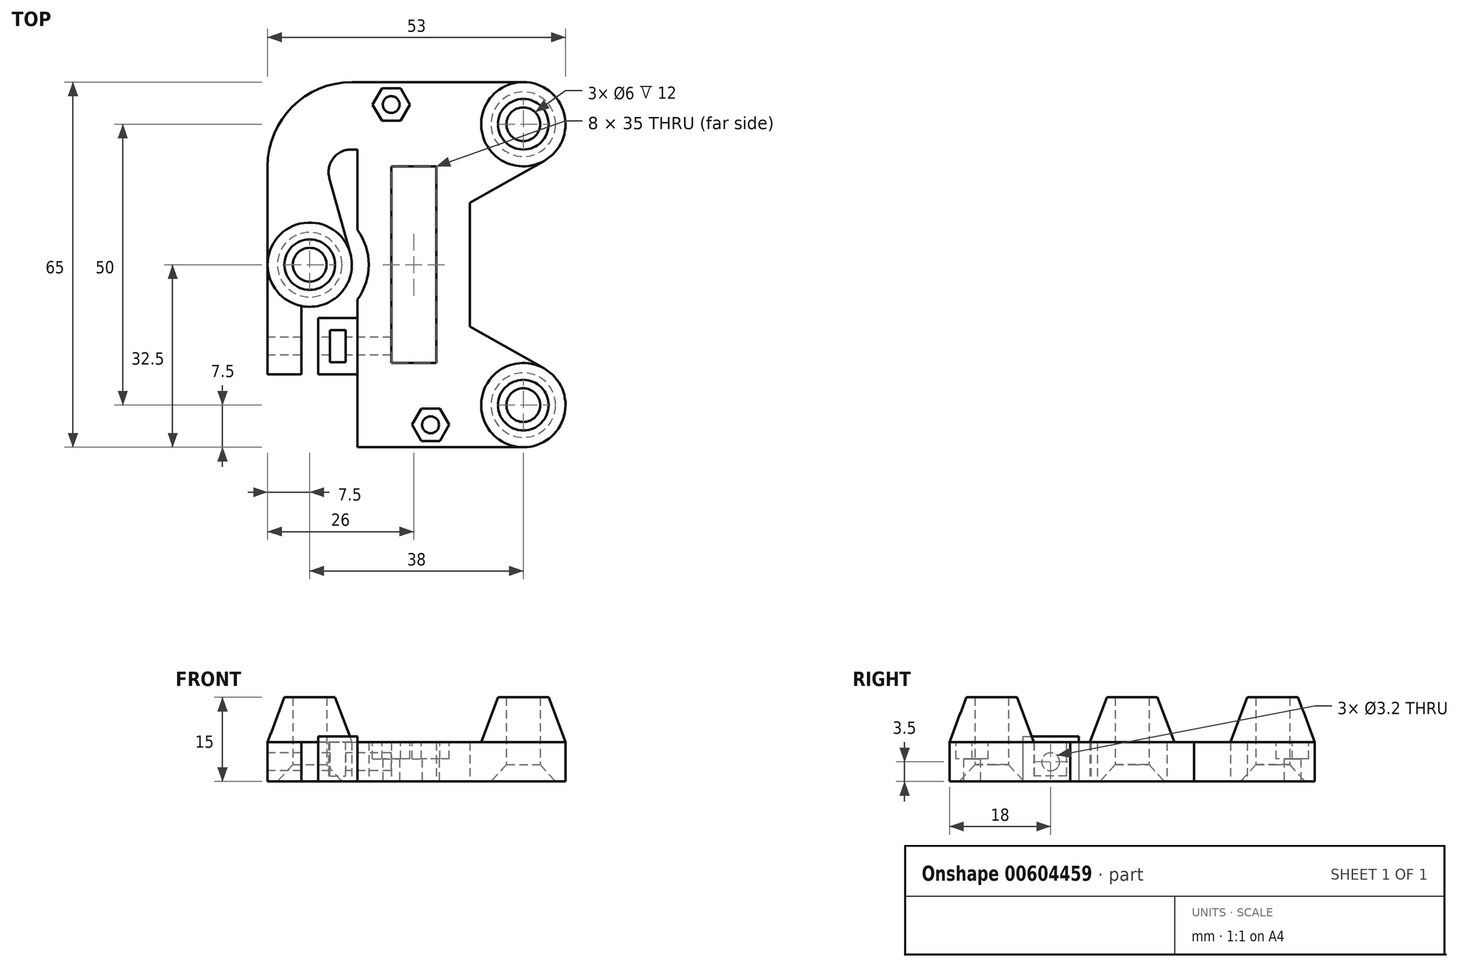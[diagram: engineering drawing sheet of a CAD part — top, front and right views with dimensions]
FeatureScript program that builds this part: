
annotation { "Feature Type Name" : "Feature", "Feature Type Description" : "" }
export const myFeature = defineFeature(function(context is Context, id is Id, definition is map)
    precondition{}
    {
        {
            var Q0;
            Q0=qCreatedBy(makeId("Top.planeOp"),FACE);
            var sketch = newSketch(context, id + "F0", { "sketchPlane" : qUnion([Q0])});
            skLineSegment(sketch, "E0.bottom", {"start": v(0, 0) * mm, "end": v(20, 0) * mm});
            skLineSegment(sketch, "E0.top", {"start": v(0, 65) * mm, "end": v(20, 65) * mm});
            skLineSegment(sketch, "E0.left", {"start": v(0, 0) * mm, "end": v(0, 26.34) * mm});
            skLineSegment(sketch, "E0.right", {"start": v(20, 0) * mm, "end": v(20, 65) * mm});
            skLineSegment(sketch, "E1.bottom", {"start": v(6, 50) * mm, "end": v(14, 50) * mm});
            skLineSegment(sketch, "E1.top", {"start": v(6, 15) * mm, "end": v(14, 15) * mm});
            skLineSegment(sketch, "E1.left", {"start": v(6, 50) * mm, "end": v(6, 15) * mm});
            skLineSegment(sketch, "E1.right", {"start": v(14, 50) * mm, "end": v(14, 15) * mm});
            skLineSegment(sketch, "E2.bottom", {"start": v(-7, 23) * mm, "end": v(0, 23) * mm});
            skLineSegment(sketch, "E2.top", {"start": v(-7, 13) * mm, "end": v(0, 13) * mm});
            skLineSegment(sketch, "E2.left", {"start": v(-7, 23) * mm, "end": v(-7, 13) * mm});
            skLineSegment(sketch, "E2.right", {"start": v(0, 23) * mm, "end": v(0, 13) * mm});
            skCircle(sketch, "E3", {"center": v(29.5, 7.5) * mm, "radius": 3 * mm});
            skCircle(sketch, "E4", {"center": v(29.5, 57.5) * mm, "radius": 3 * mm});
            skCircle(sketch, "E5", {"center": v(-8.5, 32.5) * mm, "radius": 7.5 * mm});
            skCircle(sketch, "E6", {"center": v(29.5, 57.5) * mm, "radius": 7.5 * mm});
            skCircle(sketch, "E7", {"center": v(29.5, 7.5) * mm, "radius": 7.5 * mm});
            skLineSegment(sketch, "E8", {"start": v(20, 0) * mm, "end": v(29.5, 0) * mm});
            skLineSegment(sketch, "E9", {"start": v(20, 65) * mm, "end": v(29.5, 65) * mm});
            skLineSegment(sketch, "E10", {"start": v(-1.27, 34.5) * mm, "end": v(-5, 47.93) * mm});
            skLineSegment(sketch, "E11", {"start": v(-16, 13) * mm, "end": v(-16, 50) * mm});
            skCircle(sketch, "E12", {"center": v(-8.5, 32.5) * mm, "radius": 3 * mm});
            skLineSegment(sketch, "E13", {"start": v(-16, 13) * mm, "end": v(-10, 13) * mm});
            skLineSegment(sketch, "E14", {"start": v(-10, 13) * mm, "end": v(-10, 25.15) * mm});
            skLineSegment(sketch, "E15", {"start": v(-1, 65) * mm, "end": v(0, 65) * mm});
            skCircle(sketch, "E16", {"center": v(6, 61) * mm, "radius": 1.5 * mm});
            skCircle(sketch, "E17", {"center": v(13, 4) * mm, "radius": 1.5 * mm});
            skLineSegment(sketch, "E18", {"start": v(33.2, 50.97) * mm, "end": v(20, 43.5) * mm});
            skLineSegment(sketch, "E19", {"start": v(33.2, 14.03) * mm, "end": v(20, 21.5) * mm});
            skPoint(sketch, "E20.visualSharp", {"position": v(-16, 65) * mm});
            skArc(sketch, "E20.filletArc", {"start": v(-1, 65) * mm, "mid": v(-11.6, 60.6) * mm, "end": v(-16, 50) * mm});
            skLineSegment(sketch, "E21", {"start": v(-1.15, 53) * mm, "end": v(0, 53) * mm});
            skPoint(sketch, "E22", {"position": v(20, 32.5) * mm});
            skArc(sketch, "E23", {"start": v(0, 26.34) * mm, "mid": v(2, 32.5) * mm, "end": v(0, 38.66) * mm});
            skLineSegment(sketch, "E24", {"start": v(6, 32.5) * mm, "end": v(2, 32.5) * mm});
            skLineSegment(sketch, "E25.trimOffspring", {"start": v(0, 38.66) * mm, "end": v(0, 65) * mm});
            skPoint(sketch, "E26.visualSharp", {"position": v(-6.4, 53) * mm});
            skArc(sketch, "E26.filletArc", {"start": v(-1.15, 53) * mm, "mid": v(-4.33, 51.42) * mm, "end": v(-5, 47.93) * mm});
            skPoint(sketch, "E27", {"position": v(37, 57.5) * mm});
            skSolve(sketch);
        }
        {
            var Q0;
            Q0=qSketchRegion(id+"F0",true);
            extrude(context, id + "F1", {"entities" : qUnion([Q0]), "depth" : 7 * mm});
        }
        {
            var Q0;
            Q0=makeQuery(id+"F1.opExtrude","CAP_FACE",FACE,{"disambiguationData":[OSD([sQuery(id+"F0.wireOp",EDGE,"E0.bottom"),sQuery(id+"F0.wireOp",EDGE,"E0.top"),sQuery(id+"F0.wireOp",EDGE,"E0.left"),sQuery(id+"F0.wireOp",EDGE,"E0.right"),sQuery(id+"F0.wireOp",EDGE,"E1.bottom"),sQuery(id+"F0.wireOp",EDGE,"E1.top"),sQuery(id+"F0.wireOp",EDGE,"E1.left"),sQuery(id+"F0.wireOp",EDGE,"E1.right"),sQuery(id+"F0.wireOp",EDGE,"E2.bottom"),sQuery(id+"F0.wireOp",EDGE,"E2.top"),sQuery(id+"F0.wireOp",EDGE,"E2.left"),sQuery(id+"F0.wireOp",EDGE,"E3"),sQuery(id+"F0.wireOp",EDGE,"E4"),sQuery(id+"F0.wireOp",EDGE,"E5"),sQuery(id+"F0.wireOp",EDGE,"E6"),sQuery(id+"F0.wireOp",EDGE,"E7"),sQuery(id+"F0.wireOp",EDGE,"E8"),sQuery(id+"F0.wireOp",EDGE,"E9"),sQuery(id+"F0.wireOp",EDGE,"E10"),sQuery(id+"F0.wireOp",EDGE,"E11"),sQuery(id+"F0.wireOp",EDGE,"E12"),sQuery(id+"F0.wireOp",EDGE,"E13"),sQuery(id+"F0.wireOp",EDGE,"E14"),sQuery(id+"F0.wireOp",EDGE,"E16"),sQuery(id+"F0.wireOp",EDGE,"E17"),sQuery(id+"F0.wireOp",EDGE,"E18"),sQuery(id+"F0.wireOp",EDGE,"E19"),sQuery(id+"F0.wireOp",EDGE,"E20.filletArc"),sQuery(id+"F0.wireOp",EDGE,"E23"),sQuery(id+"F0.wireOp",EDGE,"E25.trimOffspring"),sQuery(id+"F0.wireOp",EDGE,"E26.filletArc")])],"isStart":false});
            cPlane(context, id + "F2", {"entities" : qUnion([Q0]), "cplaneType" : CPlaneType.OFFSET, "offset" : 0 * mm, "width" : 150 * mm, "height" : 150 * mm});
        }
        {
            var Q0;
            Q0=qCreatedBy(id+"F2.planeOp",FACE);
            var sketch = newSketch(context, id + "F3", { "sketchPlane" : qUnion([Q0])});
            skCircle(sketch, "E28.cCircle", {"center": v(13, 4) * mm, "radius": 2.88 * mm, "construction": true});
            skLineSegment(sketch, "E28.0", {"start": v(14.66, 1.13) * mm, "end": v(11.34, 1.12) * mm});
            skLineSegment(sketch, "E28.1", {"start": v(11.34, 1.12) * mm, "end": v(9.68, 4) * mm});
            skLineSegment(sketch, "E28.2", {"start": v(9.68, 4) * mm, "end": v(11.34, 6.88) * mm});
            skLineSegment(sketch, "E28.3", {"start": v(11.34, 6.88) * mm, "end": v(14.66, 6.88) * mm});
            skLineSegment(sketch, "E28.4", {"start": v(14.66, 6.87) * mm, "end": v(16.32, 4) * mm});
            skLineSegment(sketch, "E28.5", {"start": v(16.32, 4) * mm, "end": v(14.66, 1.12) * mm});
            skPoint(sketch, "E28.0.midPoint", {"position": v(13, 1.13) * mm});
            skCircle(sketch, "E29.cCircle", {"center": v(6, 61) * mm, "radius": 2.88 * mm, "construction": true});
            skLineSegment(sketch, "E29.0", {"start": v(9.32, 61) * mm, "end": v(7.66, 58.13) * mm});
            skLineSegment(sketch, "E29.1", {"start": v(7.66, 58.12) * mm, "end": v(4.34, 58.12) * mm});
            skLineSegment(sketch, "E29.2", {"start": v(4.34, 58.12) * mm, "end": v(2.68, 61) * mm});
            skLineSegment(sketch, "E29.3", {"start": v(2.68, 61) * mm, "end": v(4.34, 63.87) * mm});
            skLineSegment(sketch, "E29.4", {"start": v(4.34, 63.88) * mm, "end": v(7.66, 63.88) * mm});
            skLineSegment(sketch, "E29.5", {"start": v(7.66, 63.88) * mm, "end": v(9.32, 61) * mm});
            skPoint(sketch, "E29.0.midPoint", {"position": v(8.49, 59.56) * mm});
            skSolve(sketch);
        }
        {
            var Q0;
            Q0=qSketchRegion(id+"F3",true);
            extrude(context, id + "F4", {"entities" : qUnion([Q0]), "operationType" : NewBodyOperationType.REMOVE, "oppositeDirection" : true, "depth" : 3 * mm});
        }
        {
            var Q0;
            Q0=qCreatedBy(id+"F2.planeOp",FACE);
            var sketch = newSketch(context, id + "F5", { "sketchPlane" : qUnion([Q0])});
            skLineSegment(sketch, "E30.bottom", {"start": v(-7, 13) * mm, "end": v(0, 13) * mm});
            skLineSegment(sketch, "E30.top", {"start": v(-7, 23) * mm, "end": v(0, 23) * mm});
            skLineSegment(sketch, "E30.left", {"start": v(-7, 13) * mm, "end": v(-7, 23) * mm});
            skLineSegment(sketch, "E30.right", {"start": v(0, 13) * mm, "end": v(0, 23) * mm});
            skSolve(sketch);
        }
        {
            var Q0;
            Q0=qSketchRegion(id+"F5",true);
            extrude(context, id + "F6", {"entities" : qUnion([Q0]), "operationType" : NewBodyOperationType.ADD, "depth" : 1 * mm});
        }
        {
            var Q0;
            Q0=makeQuery(id+"F6.opExtrude","CAP_FACE",FACE,{"disambiguationData":[OSD([sQuery(id+"F5.wireOp",EDGE,"E30.bottom"),sQuery(id+"F5.wireOp",EDGE,"E30.top"),sQuery(id+"F5.wireOp",EDGE,"E30.left"),sQuery(id+"F5.wireOp",EDGE,"E30.right")])],"isStart":false});
            cPlane(context, id + "F7", {"entities" : qUnion([Q0]), "cplaneType" : CPlaneType.OFFSET, "offset" : 0 * mm, "width" : 150 * mm, "height" : 150 * mm});
        }
        {
            var Q0;
            Q0=qCreatedBy(id+"F7.planeOp",FACE);
            var sketch = newSketch(context, id + "F8", { "sketchPlane" : qUnion([Q0])});
            skLineSegment(sketch, "E31.bottom", {"start": v(-4.87, 20.88) * mm, "end": v(-2.12, 20.88) * mm});
            skLineSegment(sketch, "E31.top", {"start": v(-4.87, 15.13) * mm, "end": v(-2.12, 15.13) * mm});
            skLineSegment(sketch, "E31.left", {"start": v(-4.87, 20.88) * mm, "end": v(-4.87, 15.12) * mm});
            skLineSegment(sketch, "E31.right", {"start": v(-2.12, 20.88) * mm, "end": v(-2.12, 15.12) * mm});
            skPoint(sketch, "E32", {"position": v(-2.12, 18) * mm});
            skPoint(sketch, "E33", {"position": v(-3.5, 20.88) * mm});
            skSolve(sketch);
        }
        {
            var Q0;
            Q0=makeQuery(id+"F8.imprint","IMPRINT",FACE,{"disambiguationData":[TD([[makeQuery(id+"F8.imprint","IMPRINT",EDGE,{"derivedFrom":sQuery(id+"F8.wireOp",EDGE,"E31.bottom")}),-1.0]])]});
            extrude(context, id + "F9", {"entities" : qUnion([Q0]), "operationType" : NewBodyOperationType.REMOVE, "oppositeDirection" : true, "depth" : 7 * mm});
        }
        {
            var Q0;
            Q0=makeQuery(id+"F1.opExtrude","SWEPT_FACE",FACE,{"disambiguationData":[OSD([sQuery(id+"F0.wireOp",EDGE,"E11")])]});
            cPlane(context, id + "F10", {"entities" : qUnion([Q0]), "cplaneType" : CPlaneType.OFFSET, "offset" : 0 * mm, "width" : 150 * mm, "height" : 150 * mm});
        }
        {
            var Q0;
            Q0=qCreatedBy(id+"F10.planeOp",FACE);
            var sketch = newSketch(context, id + "F11", { "sketchPlane" : qUnion([Q0])});
            skCircle(sketch, "E34", {"center": v(-18, 3.5) * mm, "radius": 1.6 * mm});
            skSolve(sketch);
        }
        {
            var Q0;
            Q0=qSketchRegion(id+"F11",true);
            var Q1;
            Q1=makeQuery(id+"F1.opExtrude","SWEPT_FACE",FACE,{"disambiguationData":[OSD([sQuery(id+"F0.wireOp",EDGE,"E1.right")])]});
            extrude(context, id + "F12", {"entities" : qUnion([Q0]), "operationType" : NewBodyOperationType.REMOVE, "endBound" : BoundingType.UP_TO_SURFACE, "oppositeDirection" : true, "endBoundEntityFace" : qUnion([Q1]), "depth" : 25 * mm});
        }
        {
            var Q0;
            Q0=makeQuery(id+"F1.opExtrude","SWEPT_FACE",FACE,{"disambiguationData":[OSD([sQuery(id+"F0.wireOp",EDGE,"E0.right")])]});
            var Q1;
            Q1=sQuery(id+"F0.wireOp",VERTEX,"E3.center");
            cPlane(context, id + "F13", {"entities" : qUnion([Q0, Q1]), "cplaneType" : CPlaneType.PLANE_POINT, "offset" : 8 * mm, "width" : 150 * mm, "height" : 150 * mm});
        }
        {
            var Q0;
            Q0=qCreatedBy(id+"F13.planeOp",FACE);
            var sketch = newSketch(context, id + "F14", { "sketchPlane" : qUnion([Q0])});
            skLineSegment(sketch, "E35", {"start": v(7.5, 15) * mm, "end": v(7.5, 0) * mm});
            skLineSegment(sketch, "E36", {"start": v(57.5, 15) * mm, "end": v(57.5, 0) * mm});
            skLineSegment(sketch, "E37", {"start": v(0, 7) * mm, "end": v(4.5, 7) * mm});
            skLineSegment(sketch, "E38", {"start": v(4.5, 7) * mm, "end": v(4.5, 15) * mm});
            skLineSegment(sketch, "E39", {"start": v(4.5, 15) * mm, "end": v(3, 15) * mm});
            skLineSegment(sketch, "E40", {"start": v(3, 15) * mm, "end": v(0, 7) * mm});
            skLineSegment(sketch, "E41", {"start": v(60.5, 7) * mm, "end": v(65, 7) * mm});
            skLineSegment(sketch, "E42", {"start": v(65, 7) * mm, "end": v(62, 15) * mm});
            skLineSegment(sketch, "E43", {"start": v(62, 15) * mm, "end": v(60.5, 15) * mm});
            skLineSegment(sketch, "E44", {"start": v(60.5, 15) * mm, "end": v(60.5, 7) * mm});
            skLineSegment(sketch, "E45", {"start": v(1.75, 0) * mm, "end": v(4.5, 3) * mm});
            skLineSegment(sketch, "E46", {"start": v(4.5, 3) * mm, "end": v(4.5, 0) * mm});
            skLineSegment(sketch, "E47", {"start": v(4.5, 0) * mm, "end": v(1.75, 0) * mm});
            skLineSegment(sketch, "E48", {"start": v(63.25, 0) * mm, "end": v(60.5, 3) * mm});
            skLineSegment(sketch, "E49", {"start": v(60.5, 3) * mm, "end": v(60.5, 0) * mm});
            skLineSegment(sketch, "E50", {"start": v(60.5, 0) * mm, "end": v(63.25, 0) * mm});
            skSolve(sketch);
        }
        {
            var Q0;
            Q0=makeQuery(id+"F14.imprint","IMPRINT",FACE,{"disambiguationData":[TD([[makeQuery(id+"F14.imprint","IMPRINT",EDGE,{"derivedFrom":sQuery(id+"F14.wireOp",EDGE,"E37")}),1.0]])]});
            var Q1;
            Q1=sQuery(id+"F14.wireOp",EDGE,"E35");
            revolve(context, id + "F15", {"operationType" : NewBodyOperationType.ADD, "entities" : qUnion([Q0]), "axis" : qUnion([Q1]), "revolveType" : RevolveType.FULL});
        }
        {
            var Q0;
            Q0=makeQuery(id+"F14.imprint","IMPRINT",FACE,{"disambiguationData":[TD([[makeQuery(id+"F14.imprint","IMPRINT",EDGE,{"derivedFrom":sQuery(id+"F14.wireOp",EDGE,"E41")}),1.0]])]});
            var Q1;
            Q1=sQuery(id+"F14.wireOp",EDGE,"E36");
            revolve(context, id + "F16", {"operationType" : NewBodyOperationType.ADD, "entities" : qUnion([Q0]), "axis" : qUnion([Q1]), "revolveType" : RevolveType.FULL});
        }
        {
            var Q0;
            Q0=makeQuery(id+"F14.imprint","IMPRINT",FACE,{"disambiguationData":[TD([[makeQuery(id+"F14.imprint","IMPRINT",EDGE,{"derivedFrom":sQuery(id+"F14.wireOp",EDGE,"E45")}),-1.0]])]});
            var Q1;
            Q1=sQuery(id+"F14.wireOp",EDGE,"E46");
            var Q2;
            Q2=sQuery(id+"F14.wireOp",EDGE,"E45");
            var Q3;
            Q3=sQuery(id+"F14.wireOp",EDGE,"E47");
            var Q4;
            Q4=sQuery(id+"F14.wireOp",EDGE,"E35");
            revolve(context, id + "F17", {"operationType" : NewBodyOperationType.REMOVE, "entities" : qUnion([Q0]), "surfaceEntities" : qUnion([Q1, Q2, Q3]), "axis" : qUnion([Q4]), "revolveType" : RevolveType.FULL, "oppositeDirection" : true});
        }
        {
            var Q0;
            Q0=makeQuery(id+"F14.imprint","IMPRINT",FACE,{"disambiguationData":[TD([[makeQuery(id+"F14.imprint","IMPRINT",EDGE,{"derivedFrom":sQuery(id+"F14.wireOp",EDGE,"E48")}),1.0]])]});
            var Q1;
            Q1=sQuery(id+"F14.wireOp",EDGE,"E36");
            revolve(context, id + "F18", {"operationType" : NewBodyOperationType.REMOVE, "entities" : qUnion([Q0]), "axis" : qUnion([Q1]), "revolveType" : RevolveType.FULL, "oppositeDirection" : true});
        }
        {
            var Q0;
            Q0=makeQuery(id+"F1.opExtrude","SWEPT_FACE",FACE,{"disambiguationData":[OSD([sQuery(id+"F0.wireOp",EDGE,"E11")])]});
            var Q1;
            Q1=sQuery(id+"F0.wireOp",VERTEX,"E12.center");
            cPlane(context, id + "F19", {"entities" : qUnion([Q0, Q1]), "cplaneType" : CPlaneType.PLANE_POINT, "offset" : 25 * mm, "width" : 150 * mm, "height" : 150 * mm});
        }
        {
            var Q0;
            Q0=qCreatedBy(id+"F19.planeOp",FACE);
            var sketch = newSketch(context, id + "F20", { "sketchPlane" : qUnion([Q0])});
            skLineSegment(sketch, "E51", {"start": v(-32.5, 15) * mm, "end": v(-32.5, 0) * mm});
            skLineSegment(sketch, "E52", {"start": v(-29.5, 0) * mm, "end": v(-29.5, 3) * mm});
            skLineSegment(sketch, "E53", {"start": v(-29.5, 3) * mm, "end": v(-26.75, 0) * mm});
            skLineSegment(sketch, "E54", {"start": v(-26.75, 0) * mm, "end": v(-29.5, 0) * mm});
            skLineSegment(sketch, "E55", {"start": v(-29.5, 7) * mm, "end": v(-29.5, 15) * mm});
            skLineSegment(sketch, "E56", {"start": v(-29.5, 15) * mm, "end": v(-28, 15) * mm});
            skLineSegment(sketch, "E57", {"start": v(-28, 15) * mm, "end": v(-25, 7) * mm});
            skLineSegment(sketch, "E58", {"start": v(-25, 7) * mm, "end": v(-29.5, 7) * mm});
            skSolve(sketch);
        }
        {
            var Q0;
            Q0=makeQuery(id+"F20.imprint","IMPRINT",FACE,{"disambiguationData":[TD([[makeQuery(id+"F20.imprint","IMPRINT",EDGE,{"derivedFrom":sQuery(id+"F20.wireOp",EDGE,"E55")}),-1.0]])]});
            var Q1;
            Q1=sQuery(id+"F20.wireOp",EDGE,"E51");
            revolve(context, id + "F21", {"operationType" : NewBodyOperationType.ADD, "entities" : qUnion([Q0]), "axis" : qUnion([Q1]), "revolveType" : RevolveType.FULL});
        }
        {
            var Q0;
            Q0=makeQuery(id+"F20.imprint","IMPRINT",FACE,{"disambiguationData":[TD([[makeQuery(id+"F20.imprint","IMPRINT",EDGE,{"derivedFrom":sQuery(id+"F20.wireOp",EDGE,"E52")}),-1.0]])]});
            var Q1;
            Q1=sQuery(id+"F20.wireOp",EDGE,"E51");
            revolve(context, id + "F22", {"operationType" : NewBodyOperationType.REMOVE, "entities" : qUnion([Q0]), "axis" : qUnion([Q1]), "revolveType" : RevolveType.FULL, "oppositeDirection" : true});
        }
    });
